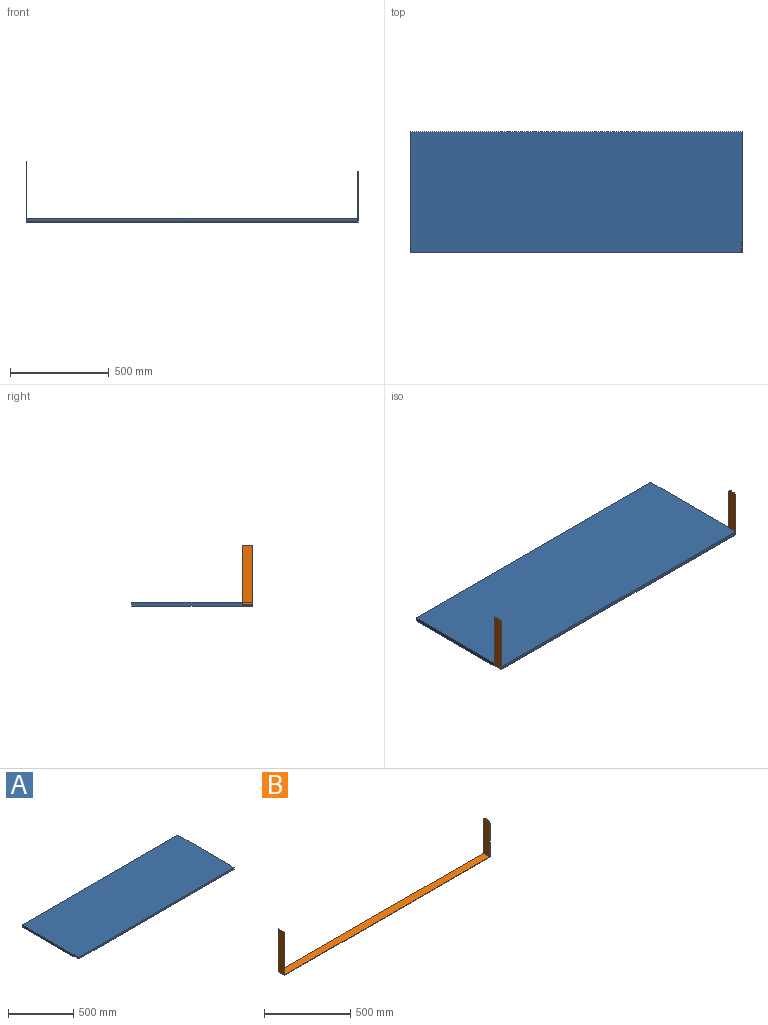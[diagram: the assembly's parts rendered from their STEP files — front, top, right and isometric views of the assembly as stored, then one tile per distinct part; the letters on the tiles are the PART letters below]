
ASSEMBLY  parts=2 mates=1
PART A: 12 faces, bbox 1684.3x609.6x19.1 mm
  f0: plane 1677.99x15.88mm, normal (0,-1,0), area 26635.8mm2, adj f1,f3,f8,f9,f10,f11
  f1: plane 1684.34x609.6mm, normal (0,0,1), area 1026449.6mm2, adj f0,f2,f5,f6,f7,f8,f9
  f2: plane 558.8x19.05mm, normal (-1,0,0), area 10645.1mm2, adj f1,f4,f6,f7
  f3: plane 1673.42x50.8mm, normal (0,0,-1), area 85009.5mm2, adj f0,f7,f10,f11
  f4: plane 1684.34x558.8mm, normal (0,0,-1), area 941207.8mm2, adj f2,f5,f6,f7
  f5: plane 558.8x19.05mm, normal (1,0,0), area 10645.1mm2, adj f1,f4,f6,f7
  f6: plane 1684.34x19.05mm, normal (0,1,0), area 32086.6mm2, adj f1,f2,f4,f5
  f7: plane 1684.34x19.05mm, normal (0,-1,0), area 5450.8mm2, adj f1,f2,f3,f4,f5,f8,f9,f10
  f8: plane 50.8x13.59mm, normal (-1,0,0), area 690.3mm2, adj f0,f1,f7,f11
  f9: plane 50.8x13.59mm, normal (1,0,0), area 690.3mm2, adj f0,f1,f7,f10
  f10: cylinder r=2.29mm len=50.8mm, axis (0,1,0), area 182.4mm2, adj f0,f3,f7,f9
  f11: cylinder r=2.29mm len=50.8mm, axis (0,1,0), area 182.4mm2, adj f0,f3,f7,f8
PART B: 24 faces, bbox 1684.3x50.8x304.8 mm
  f0: plane 299.34x3.18mm, normal (0,-1,0), area 950.4mm2, adj f1,f3,f4,f21
  f1: plane 50.8x3.18mm, normal (0,0,1), area 161.3mm2, adj f0,f2,f3,f4
  f2: plane 299.34x3.18mm, normal (0,1,0), area 950.4mm2, adj f1,f3,f4,f20
  f3: plane 299.34x50.8mm, normal (-1,0,0), area 15206.4mm2, adj f0,f1,f2,f22
  f4: plane 299.34x50.8mm, normal (1,0,0), area 15206.4mm2, adj f0,f1,f2,f23
  f5: plane 1673.42x3.18mm, normal (0,-1,0), area 5313.1mm2, adj f7,f8,f17,f21
  f6: plane 1673.42x3.18mm, normal (0,1,0), area 5313.1mm2, adj f7,f8,f16,f20
  f7: plane 1673.42x50.8mm, normal (0,0,-1), area 85009.5mm2, adj f5,f6,f18,f22
  f8: plane 1673.42x50.8mm, normal (0,0,1), area 85009.5mm2, adj f5,f6,f19,f23
  f9: plane 229.49x3.18mm, normal (0,-1,0), area 728.6mm2, adj f12,f13,f14,f17
  f10: plane 229.49x3.18mm, normal (0,1,0), area 728.6mm2, adj f12,f13,f15,f16
  f11: plane 12.7x3.18mm, normal (0,0,1), area 40.3mm2, adj f12,f13,f14,f15
  f12: plane 248.54x50.8mm, normal (1,0,0), area 12470mm2, adj f9,f10,f11,f14,f15,f18
  f13: plane 248.54x50.8mm, normal (-1,0,0), area 12470mm2, adj f9,f10,f11,f14,f15,f19
  f14: cylinder r=19.05mm len=19.05mm, axis (1,0,0), area 95mm2, adj f9,f11,f12,f13
  f15: cylinder r=19.05mm len=19.05mm, axis (-1,0,0), area 95mm2, adj f10,f11,f12,f13
  f16: plane 5.46x5.46mm, normal (0,1,0), area 19.3mm2, adj f6,f10,f18,f19
  f17: plane 5.46x5.46mm, normal (0,-1,0), area 19.3mm2, adj f5,f9,f18,f19
  f18: cylinder r=5.46mm len=50.8mm, axis (0,1,0), area 435.8mm2, adj f7,f12,f16,f17
  f19: cylinder r=2.29mm len=50.8mm, axis (0,1,0), area 182.4mm2, adj f8,f13,f16,f17
  f20: plane 5.46x5.46mm, normal (0,1,0), area 19.3mm2, adj f2,f6,f22,f23
  f21: plane 5.46x5.46mm, normal (0,-1,0), area 19.3mm2, adj f0,f5,f22,f23
  f22: cylinder r=5.46mm len=50.8mm, axis (0,1,0), area 435.8mm2, adj f3,f7,f20,f21
  f23: cylinder r=2.29mm len=50.8mm, axis (0,1,0), area 182.4mm2, adj f4,f8,f20,f21
PLACE A t=(-425.12,174.39,211.48)mm
PLACE B t=(-425.12,174.39,211.48)mm
MATE fastened A.f3 <-> B.f8  axis (0,0,-1) through (417.05,174.39,214.66)mm
